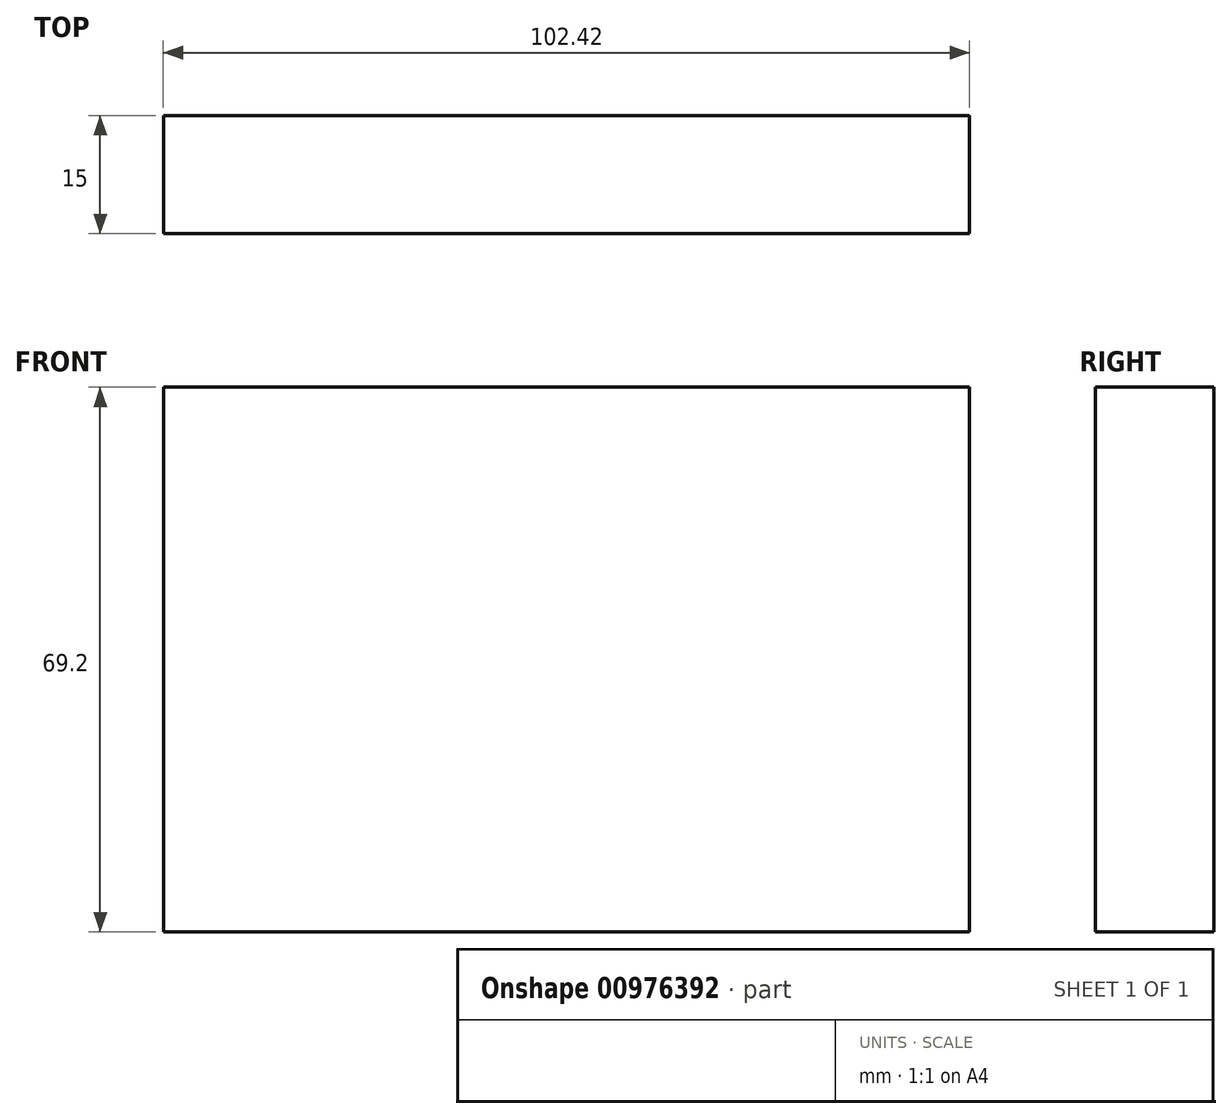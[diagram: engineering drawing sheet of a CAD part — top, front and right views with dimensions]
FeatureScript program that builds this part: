
annotation { "Feature Type Name" : "Feature", "Feature Type Description" : "" }
export const myFeature = defineFeature(function(context is Context, id is Id, definition is map)
    precondition{}
    {
        {
            var Q0;
            Q0=qCreatedBy(makeId("Front.planeOp"),FACE);
            var sketch = newSketch(context, id + "F0", { "sketchPlane" : qUnion([Q0])});
            skLineSegment(sketch, "E0.bottom", {"start": v(51.2, 34.6) * mm, "end": v(-51.2, 34.6) * mm});
            skLineSegment(sketch, "E0.top", {"start": v(51.2, -34.6) * mm, "end": v(-51.2, -34.6) * mm});
            skLineSegment(sketch, "E0.left", {"start": v(51.2, 34.6) * mm, "end": v(51.2, -34.6) * mm});
            skLineSegment(sketch, "E0.right", {"start": v(-51.2, 34.6) * mm, "end": v(-51.2, -34.6) * mm});
            skPoint(sketch, "E0.middle", {"position": v(0, 0) * mm});
            skSolve(sketch);
        }
        {
            var Q0;
            Q0 = qSketchRegion(id + "F0", true);
            extrude(context, id + "F1", {"entities" : qUnion([Q0]), "depth" : 15 * mm, "offsetDistance" : 25.4 * mm});
        }
        {
            var Q0;
            Q0=qCreatedBy(makeId("Front.planeOp"),FACE);
            var sketch = newSketch(context, id + "F2", { "sketchPlane" : qUnion([Q0])});
            skCircle(sketch, "E1", {"center": v(0, 0) * mm, "radius": 30.07 * mm});
            skSolve(sketch);
        }
        {
            var Q0;
            Q0=sQuery(id+"F2.wireOp",EDGE,"E1");
            extrude(context, id + "F3", {"bodyType" : ToolBodyType.SURFACE, "surfaceEntities" : qUnion([Q0]), "depth" : 330.2 * mm, "offsetDistance" : 25.4 * mm});
        }
        {
            var Q0;
            Q0=makeQuery(id+"F1.opExtrude","CAP_FACE",FACE,{"disambiguationData":[OSD([sQuery(id+"F0.wireOp",EDGE,"E0.bottom"),sQuery(id+"F0.wireOp",EDGE,"E0.top"),sQuery(id+"F0.wireOp",EDGE,"E0.left"),sQuery(id+"F0.wireOp",EDGE,"E0.right")])],"isStart":true});
            var sketch = newSketch(context, id + "F4", { "sketchPlane" : qUnion([Q0])});
            skLineSegment(sketch, "E2.bottom", {"start": v(15.65, 11.36) * mm, "end": v(-17.91, 11.36) * mm});
            skLineSegment(sketch, "E2.top", {"start": v(15.65, -14.98) * mm, "end": v(-17.91, -14.98) * mm});
            skLineSegment(sketch, "E2.left", {"start": v(15.65, 11.36) * mm, "end": v(15.65, -14.98) * mm});
            skLineSegment(sketch, "E2.right", {"start": v(-17.91, 11.36) * mm, "end": v(-17.91, -14.98) * mm});
            skLineSegment(sketch, "E3.bottom", {"start": v(-17.91, -14.98) * mm, "end": v(0, -14.98) * mm});
            skLineSegment(sketch, "E3.top", {"start": v(-17.91, -14.98) * mm, "end": v(0, -14.98) * mm});
            skLineSegment(sketch, "E3.left", {"start": v(-17.91, -14.98) * mm, "end": v(-17.91, -14.98) * mm});
            skLineSegment(sketch, "E3.right", {"start": v(0, -14.98) * mm, "end": v(0, -14.98) * mm});
            skSolve(sketch);
        }
        {
            var Q0;
            Q0=sQuery(id+"F4.wireOp",EDGE,"E2.right");
            var Q1;
            Q1=sQuery(id+"F4.wireOp",EDGE,"E2.top");
            var Q2;
            Q2=sQuery(id+"F4.wireOp",EDGE,"E2.left");
            var Q3;
            Q3=sQuery(id+"F4.wireOp",EDGE,"E2.bottom");
            extrude(context, id + "F5", {"bodyType" : ToolBodyType.SURFACE, "surfaceEntities" : qUnion([Q0, Q1, Q2, Q3]), "depth" : 25.4 * mm, "offsetDistance" : 25.4 * mm});
        }
    });
